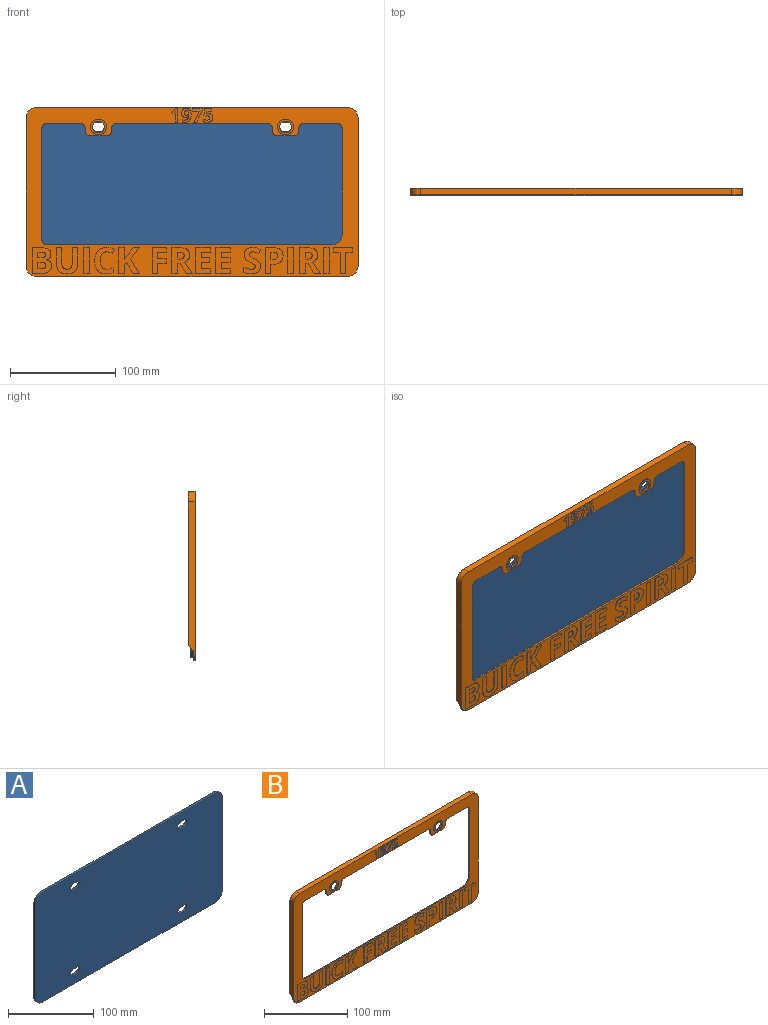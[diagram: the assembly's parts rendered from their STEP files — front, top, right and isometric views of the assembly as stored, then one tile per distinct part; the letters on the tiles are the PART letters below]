
ASSEMBLY  parts=2 mates=1
PART A: 26 faces, bbox 308x3x156 mm
  f0: plane 284x3mm, normal (0,0,1), area 852mm2, adj f1,f23,f24,f25
  f1: cylinder r=12mm len=12mm, axis (0,1,0), area 56.5mm2, adj f0,f2,f24,f25
  f2: plane 132x3mm, normal (-1,0,0), area 396mm2, adj f1,f3,f24,f25
  f3: cylinder r=12mm len=12mm, axis (0,1,0), area 56.5mm2, adj f2,f4,f24,f25
  f4: plane 284x3mm, normal (0,0,-1), area 852mm2, adj f3,f5,f24,f25
  f5: cylinder r=12mm len=12mm, axis (0,1,0), area 56.5mm2, adj f4,f6,f24,f25
  f6: plane 132x3mm, normal (1,0,0), area 396mm2, adj f5,f23,f24,f25
  f7: plane 8x3mm, normal (0,0,-1), area 24mm2, adj f8,f19,f24,f25
  f8: cylinder r=4.25mm len=8.5mm, axis (0,1,0), area 40.1mm2, adj f7,f9,f24,f25
  f9: plane 8x3mm, normal (0,0,1), area 24mm2, adj f8,f19,f24,f25
  f10: cylinder r=4.25mm len=8.5mm, axis (0,1,0), area 40.1mm2, adj f11,f20,f24,f25
  f11: plane 8x3mm, normal (0,0,1), area 24mm2, adj f10,f12,f24,f25
  f12: cylinder r=4.25mm len=8.5mm, axis (0,1,0), area 40.1mm2, adj f11,f20,f24,f25
  f13: plane 8x3mm, normal (0,0,-1), area 24mm2, adj f14,f21,f24,f25
  f14: cylinder r=4.25mm len=8.5mm, axis (0,1,0), area 40.1mm2, adj f13,f15,f24,f25
  f15: plane 8x3mm, normal (0,0,1), area 24mm2, adj f14,f21,f24,f25
  f16: cylinder r=4.25mm len=8.5mm, axis (0,1,0), area 40.1mm2, adj f17,f22,f24,f25
  f17: plane 8x3mm, normal (0,0,-1), area 24mm2, adj f16,f18,f24,f25
  f18: cylinder r=4.25mm len=8.5mm, axis (0,1,0), area 40.1mm2, adj f17,f22,f24,f25
  f19: cylinder r=4.25mm len=8.5mm, axis (0,1,0), area 40.1mm2, adj f7,f9,f24,f25
  f20: plane 8x3mm, normal (0,0,-1), area 24mm2, adj f10,f12,f24,f25
  f21: cylinder r=4.25mm len=8.5mm, axis (0,1,0), area 40.1mm2, adj f13,f15,f24,f25
  f22: plane 8x3mm, normal (0,0,1), area 24mm2, adj f16,f18,f24,f25
  f23: cylinder r=12mm len=12mm, axis (0,1,0), area 56.5mm2, adj f0,f6,f24,f25
  f24: plane 308x156mm, normal (0,-1,0), area 47425.4mm2, adj f0,f1,f2,f3,f4,f5,f6,f7
  f25: plane 308x156mm, normal (0,1,0), area 47425.4mm2, adj f0,f1,f2,f3,f4,f5,f6,f7
PART B: 350 faces, bbox 314x7x160 mm
  f0: plane 140x4.8mm, normal (1,0,0), area 564mm2, adj f1,f329,f334,f335,f340,f342,f343,f345
  f1: plane 314x158mm, normal (0,1,0), area 16737.1mm2, adj f0,f3,f4,f8,f9,f10,f12,f13
  f2: plane 314x160mm, normal (0,-1,0), area 13997.6mm2, adj f3,f4,f5,f6,f7,f8,f9,f10
  f3: plane 142x1.6mm, normal (0,0,-1), area 227.2mm2, adj f1,f2,f27,f33
  f4: plane 31x1.6mm, normal (0,0,-1), area 49.6mm2, adj f1,f2,f14,f31
  f5: plane 294x6.4mm, normal (0,0,1), area 1881.6mm2, adj f2,f6,f20,f335
  f6: cylinder r=10mm len=10mm, axis (0,1,0), area 100.5mm2, adj f2,f5,f7,f335
  f7: plane 140x6.4mm, normal (-1,0,0), area 887.2mm2, adj f2,f6,f8,f329,f335,f345
  f8: cylinder r=10mm len=10mm, axis (0,1,0), area 25.1mm2, adj f1,f2,f7,f9
  f9: plane 294x1.6mm, normal (0,0,-1), area 470.4mm2, adj f1,f2,f8,f10
  f10: cylinder r=10mm len=10mm, axis (0,1,0), area 25.1mm2, adj f1,f2,f9,f11
  f11: plane 140x6.4mm, normal (1,0,0), area 887.2mm2, adj f2,f10,f20,f330,f335,f344
  f12: cylinder r=5mm len=5mm, axis (0,1,0), area 12.6mm2, adj f1,f2,f13,f19
  f13: plane 105x1.6mm, normal (1,0,0), area 168mm2, adj f1,f2,f12,f14
  f14: cylinder r=5mm len=5mm, axis (0,1,0), area 12.6mm2, adj f1,f2,f4,f13
  f15: plane 31x1.6mm, normal (0,0,-1), area 49.6mm2, adj f1,f2,f16,f29
  f16: cylinder r=5mm len=5mm, axis (0,1,0), area 12.6mm2, adj f1,f2,f15,f17
  f17: plane 100x1.6mm, normal (-1,0,0), area 160mm2, adj f1,f2,f16,f18
  f18: cylinder r=10mm len=10mm, axis (0,1,0), area 25.1mm2, adj f1,f2,f17,f19
  f19: plane 269x1.6mm, normal (0,0,1), area 430.4mm2, adj f1,f2,f12,f18
  f20: cylinder r=10mm len=10mm, axis (0,1,0), area 100.5mm2, adj f2,f5,f11,f335
  f21: plane 2x1.6mm, normal (-1,0,0), area 3.2mm2, adj f1,f2,f31,f32
  f22: plane 15x1.6mm, normal (0,0,-1), area 24mm2, adj f1,f2,f32,f34
  f23: plane 2x1.6mm, normal (1,0,0), area 3.2mm2, adj f1,f2,f33,f34
  f24: plane 2x1.6mm, normal (-1,0,0), area 3.2mm2, adj f1,f2,f27,f28
  f25: plane 15x1.6mm, normal (0,0,-1), area 24mm2, adj f1,f2,f28,f30
  f26: plane 2x1.6mm, normal (1,0,0), area 3.2mm2, adj f1,f2,f29,f30
  f27: cylinder r=5mm len=5mm, axis (0,1,0), area 12.6mm2, adj f1,f2,f3,f24
  f28: cylinder r=5mm len=5mm, axis (0,-1,0), area 12.6mm2, adj f1,f2,f24,f25
  f29: cylinder r=5mm len=5mm, axis (0,-1,0), area 12.6mm2, adj f1,f2,f15,f26
  f30: cylinder r=5mm len=5mm, axis (0,1,0), area 12.6mm2, adj f1,f2,f25,f26
  f31: cylinder r=5mm len=5mm, axis (0,1,0), area 12.6mm2, adj f1,f2,f4,f21
  f32: cylinder r=5mm len=5mm, axis (0,-1,0), area 12.6mm2, adj f1,f2,f21,f22
  f33: cylinder r=5mm len=5mm, axis (0,-1,0), area 12.6mm2, adj f1,f2,f3,f23
  f34: cylinder r=5mm len=5mm, axis (0,1,0), area 12.6mm2, adj f1,f2,f22,f23
  f35: cylinder r=5.5mm len=11mm, axis (0,-1,0), area 76mm2, adj f1,f349
  f36: cylinder r=5.5mm len=11mm, axis (0,-1,0), area 76mm2, adj f1,f347
  f37: plane 2.73x0.6mm, normal (0,0,-1), area 1.6mm2, adj f2,f38,f46,f47
  f38: plane 12.89x0.6mm, normal (1,0,0), area 7.7mm2, adj f2,f37,f39,f47
  f39: plane 2.24x0.6mm, normal (0,0,1), area 1.3mm2, adj f2,f38,f40,f47
  f40: plane 4.15x3.31mm, normal (-0.62,0,0.78), area 3.2mm2, adj f2,f39,f41,f47
  f41: plane 1.64x1.31mm, normal (-0.78,0,-0.63), area 1.3mm2, adj f2,f40,f42,f47
  f42: plane 1.48x1.19mm, normal (0.63,0,-0.78), area 1.1mm2, adj f2,f41,f43,f47
  f43: extruded ~0.94x0.89mm, area 0.8mm2, adj f2,f42,f44,f47
  f44: plane 1.34x0.6mm, normal (-1,0,0.03), area 0.8mm2, adj f2,f43,f45,f47
  f45: plane 1.22x0.6mm, normal (-1,0,0.02), area 0.7mm2, adj f2,f44,f46,f47
  f46: plane 7.46x0.6mm, normal (-1,0,0), area 4.5mm2, adj f2,f37,f45,f47
  f47: plane 12.89x6.39mm, normal (0,-1,0), area 43mm2, adj f37,f38,f39,f40,f41,f42,f43,f44
  f48: extruded ~1.32x0.6mm, area 0.9mm2, adj f49,f73,f74,f75
  f49: extruded ~1.41x0.72mm, area 1mm2, adj f48,f50,f74,f75
  f50: extruded ~1.77x0.6mm, area 1.1mm2, adj f49,f51,f74,f75
  f51: extruded ~1.25x0.6mm, area 0.9mm2, adj f50,f52,f74,f75
  f52: extruded ~1.42x0.6mm, area 0.9mm2, adj f51,f53,f74,f75
  f53: extruded ~1.31x0.6mm, area 0.9mm2, adj f52,f54,f74,f75
  f54: extruded ~1.48x0.6mm, area 0.9mm2, adj f53,f73,f74,f75
  f55: extruded ~5.69x1.6mm, area 3.6mm2, adj f2,f56,f72,f74
  f56: extruded ~3.04x0.6mm, area 1.9mm2, adj f2,f55,f57,f74
  f57: extruded ~1.94x1.64mm, area 1.6mm2, adj f2,f56,f58,f74
  f58: extruded ~2.5x0.67mm, area 1.6mm2, adj f2,f57,f59,f74
  f59: extruded ~3.2x1.2mm, area 2.1mm2, adj f2,f58,f60,f74
  f60: extruded ~3.28x1.18mm, area 2.1mm2, adj f2,f59,f61,f74
  f61: extruded ~3x0.97mm, area 1.9mm2, adj f2,f60,f62,f74
  f62: extruded ~2.65x1.08mm, area 1.8mm2, adj f2,f61,f63,f74
  f63: extruded ~1.67x0.6mm, area 1mm2, adj f2,f62,f64,f74
  f64: extruded ~1.18x1.16mm, area 1mm2, adj f2,f63,f65,f74
  f65: plane 0.6x0.11mm, normal (0,0,-1), area 0.1mm2, adj f2,f64,f66,f74
  f66: extruded ~2.37x0.6mm, area 1.5mm2, adj f2,f65,f67,f74
  f67: extruded ~1.35x1.26mm, area 1.1mm2, adj f2,f66,f68,f74
  f68: extruded ~2.25x0.6mm, area 1.4mm2, adj f2,f67,f69,f74
  f69: extruded ~1.55x0.6mm, area 0.9mm2, adj f2,f68,f70,f74
  f70: plane 2.19x0.6mm, normal (-1,0,0), area 1.3mm2, adj f2,f69,f71,f74
  f71: extruded ~1.74x0.6mm, area 1mm2, adj f2,f70,f72,f74
  f72: extruded ~4.86x1.88mm, area 3.2mm2, adj f2,f55,f71,f74
  f73: extruded ~1.67x0.6mm, area 1.1mm2, adj f48,f54,f74,f75
  f74: plane 13.22x9.1mm, normal (0,-1,0), area 70.9mm2, adj f48,f49,f50,f51,f52,f53,f54,f55
  f75: plane 4.29x3.76mm, normal (0,-1,0), area 13mm2, adj f48,f49,f50,f51,f52,f53,f54,f73
  f76: plane 10.58x4.84mm, normal (-0.91,0,0.42), area 7mm2, adj f2,f77,f82,f83
  f77: plane 2.86x0.6mm, normal (0,0,-1), area 1.7mm2, adj f2,f76,f78,f83
  f78: plane 11.16x4.88mm, normal (0.92,0,-0.4), area 7.3mm2, adj f2,f77,f79,f83
  f79: plane 1.71x0.6mm, normal (1,0,0), area 1mm2, adj f2,f78,f80,f83
  f80: plane 9.25x0.6mm, normal (0,0,1), area 5.5mm2, adj f2,f79,f81,f83
  f81: plane 2.29x0.6mm, normal (-1,0,0), area 1.4mm2, adj f2,f80,f82,f83
  f82: plane 6.36x0.6mm, normal (0,0,-1), area 3.8mm2, adj f2,f76,f81,f83
  f83: plane 12.87x9.25mm, normal (0,-1,0), area 50.2mm2, adj f76,f77,f78,f79,f80,f81,f82
  f84: extruded ~2.98x1.05mm, area 1.9mm2, adj f2,f85,f103,f104
  f85: extruded ~1.33x0.6mm, area 0.8mm2, adj f2,f84,f86,f104
  f86: plane 0.6x0.31mm, normal (-0.2,0,0.98), area 0.2mm2, adj f2,f85,f87,f104
  f87: plane 2.53x0.6mm, normal (1,0,-0.09), area 1.5mm2, adj f2,f86,f88,f104
  f88: plane 4.6x0.6mm, normal (0,0,-1), area 2.8mm2, adj f2,f87,f89,f104
  f89: plane 2.31x0.6mm, normal (1,0,0), area 1.4mm2, adj f2,f88,f90,f104
  f90: plane 6.99x0.6mm, normal (0,0,1), area 4.2mm2, adj f2,f89,f91,f104
  f91: plane 6.57x0.6mm, normal (-1,0,0.07), area 4mm2, adj f2,f90,f92,f104
  f92: plane 1.09x0.6mm, normal (-0.47,0,-0.88), area 0.7mm2, adj f2,f91,f93,f104
  f93: extruded ~0.92x0.6mm, area 0.6mm2, adj f2,f92,f94,f104
  f94: extruded ~1.03x0.6mm, area 0.6mm2, adj f2,f93,f95,f104
  f95: extruded ~2.58x1.95mm, area 2.2mm2, adj f2,f94,f96,f104
  f96: extruded ~2.5x2.05mm, area 2.2mm2, adj f2,f95,f97,f104
  f97: extruded ~1.75x0.6mm, area 1.1mm2, adj f2,f96,f98,f104
  f98: extruded ~1.62x0.6mm, area 1mm2, adj f2,f97,f99,f104
  f99: plane 2.36x0.6mm, normal (-1,0,0), area 1.4mm2, adj f2,f98,f100,f104
  f100: extruded ~3.47x0.7mm, area 2.1mm2, adj f2,f99,f101,f104
  f101: extruded ~3.81x1.17mm, area 2.4mm2, adj f2,f100,f102,f104
  f102: extruded ~3.32x1.33mm, area 2.2mm2, adj f2,f101,f103,f104
  f103: extruded ~2.87x1.11mm, area 1.9mm2, adj f2,f84,f102,f104
  f104: plane 13.07x8.61mm, normal (0,-1,0), area 65.6mm2, adj f84,f85,f86,f87,f88,f89,f90,f91
  f105: plane 6.34x0.6mm, normal (1,0,0), area 3.8mm2, adj f106,f129,f130,f131
  f106: plane 3.2x0.6mm, normal (0,0,-1), area 1.9mm2, adj f105,f107,f130,f131
  f107: extruded ~4.33x3.03mm, area 3.6mm2, adj f106,f108,f130,f131
  f108: extruded ~2.5x1.02mm, area 1.7mm2, adj f107,f109,f130,f131
  f109: extruded ~3.15x0.82mm, area 2mm2, adj f108,f129,f130,f131
  f110: plane 2.99x0.6mm, normal (0,0,1), area 1.8mm2, adj f111,f127,f130,f132
  f111: plane 5.41x0.6mm, normal (1,0,0), area 3.2mm2, adj f110,f112,f130,f132
  f112: plane 2.71x0.6mm, normal (0,0,-1), area 1.6mm2, adj f111,f113,f130,f132
  f113: extruded ~3.24x0.61mm, area 2mm2, adj f112,f114,f130,f132
  f114: extruded ~2.01x1.02mm, area 1.4mm2, adj f113,f115,f130,f132
  f115: extruded ~2.15x0.94mm, area 1.5mm2, adj f114,f127,f130,f132
  f116: plane 7.58x0.6mm, normal (0,0,1), area 4.5mm2, adj f2,f117,f128,f130
  f117: plane 24.34x0.6mm, normal (-1,0,0), area 14.6mm2, adj f2,f116,f118,f130
  f118: plane 9.1x0.6mm, normal (0,0,-1), area 5.5mm2, adj f2,f117,f119,f130
  f119: extruded ~6.54x1.86mm, area 4.2mm2, adj f2,f118,f120,f130
  f120: extruded ~5.19x2.41mm, area 3.6mm2, adj f2,f119,f121,f130
  f121: extruded ~3.76x1.03mm, area 2.4mm2, adj f2,f120,f122,f130
  f122: extruded ~3.34x1.93mm, area 2.4mm2, adj f2,f121,f123,f130
  f123: plane 0.6x0.17mm, normal (1,0,0), area 0.1mm2, adj f2,f122,f124,f130
  f124: extruded ~2.72x1.68mm, area 2mm2, adj f2,f123,f125,f130
  f125: extruded ~3.58x1.02mm, area 2.3mm2, adj f2,f124,f126,f130
  f126: extruded ~4.69x2.34mm, area 3.3mm2, adj f2,f125,f128,f130
  f127: extruded ~3.04x0.65mm, area 1.9mm2, adj f110,f115,f130,f132
  f128: extruded ~7.52x1.47mm, area 4.7mm2, adj f2,f116,f126,f130
  f129: plane 3.36x0.6mm, normal (0,0,1), area 2mm2, adj f105,f109,f130,f131
  f130: plane 24.34x18.05mm, normal (0,-1,0), area 323mm2, adj f105,f106,f107,f108,f109,f110,f111,f112
  f131: plane 7.52x6.34mm, normal (0,-1,0), area 43.3mm2, adj f105,f106,f107,f108,f109,f129
  f132: plane 6.97x5.41mm, normal (0,-1,0), area 34.4mm2, adj f110,f111,f112,f113,f114,f115,f127
  f133: plane 15.75x0.6mm, normal (1,0,0), area 9.4mm2, adj f2,f134,f147,f148
  f134: plane 5.15x0.6mm, normal (0,0,1), area 3.1mm2, adj f2,f133,f135,f148
  f135: plane 14.87x0.6mm, normal (-1,0,0), area 8.9mm2, adj f2,f134,f136,f148
  f136: extruded ~4.15x1.14mm, area 2.6mm2, adj f2,f135,f137,f148
  f137: extruded ~3.67x1.32mm, area 2.4mm2, adj f2,f136,f138,f148
  f138: extruded ~3.75x1.32mm, area 2.5mm2, adj f2,f137,f139,f148
  f139: extruded ~4.13x1.13mm, area 2.6mm2, adj f2,f138,f140,f148
  f140: plane 14.9x0.6mm, normal (1,0,0), area 8.9mm2, adj f2,f139,f141,f148
  f141: plane 5.14x0.6mm, normal (0,0,1), area 3.1mm2, adj f2,f140,f142,f148
  f142: plane 15.68x0.6mm, normal (-1,0,0), area 9.4mm2, adj f2,f141,f143,f148
  f143: extruded ~6.58x2.6mm, area 4.4mm2, adj f2,f142,f144,f148
  f144: extruded ~7.29x2.41mm, area 4.7mm2, adj f2,f143,f145,f148
  f145: extruded ~5.39x1.08mm, area 3.3mm2, adj f2,f144,f146,f148
  f146: extruded ~3.49x3.11mm, area 2.8mm2, adj f2,f145,f147,f148
  f147: extruded ~4.73x1.21mm, area 3mm2, adj f2,f133,f146,f148
  f148: plane 24.68x19.98mm, normal (0,-1,0), area 271.1mm2, adj f133,f134,f135,f136,f137,f138,f139,f140
  f149: plane 24.34x0.6mm, normal (-1,0,0), area 14.6mm2, adj f2,f150,f152,f153
  f150: plane 5.16x0.6mm, normal (0,0,-1), area 3.1mm2, adj f2,f149,f151,f153
  f151: plane 24.34x0.6mm, normal (1,0,0), area 14.6mm2, adj f2,f150,f152,f153
  f152: plane 5.16x0.6mm, normal (0,0,1), area 3.1mm2, adj f2,f149,f151,f153
  f153: plane 24.34x5.16mm, normal (0,-1,0), area 125.6mm2, adj f149,f150,f151,f152
  f154: extruded ~4.51x2.19mm, area 3.1mm2, adj f2,f155,f168,f169
  f155: extruded ~2.71x0.6mm, area 1.7mm2, adj f2,f154,f156,f169
  f156: extruded ~2.75x1.13mm, area 1.8mm2, adj f2,f155,f157,f169
  f157: plane 4.2x1.66mm, normal (0.93,0,-0.37), area 2.7mm2, adj f2,f156,f158,f169
  f158: extruded ~7.12x1.71mm, area 4.4mm2, adj f2,f157,f159,f169
  f159: extruded ~6.07x1.52mm, area 3.8mm2, adj f2,f158,f160,f169
  f160: extruded ~4.38x3.97mm, area 3.6mm2, adj f2,f159,f161,f169
  f161: extruded ~6.65x1.38mm, area 4.1mm2, adj f2,f160,f162,f169
  f162: extruded ~9.25x2.81mm, area 5.9mm2, adj f2,f161,f163,f169
  f163: extruded ~8.12x3.22mm, area 5.4mm2, adj f2,f162,f164,f169
  f164: extruded ~6.69x1.25mm, area 4.1mm2, adj f2,f163,f165,f169
  f165: plane 4.33x0.6mm, normal (1,0,0), area 2.6mm2, adj f2,f164,f166,f169
  f166: extruded ~6.21x1.28mm, area 3.8mm2, adj f2,f165,f167,f169
  f167: extruded ~8.14x6.11mm, area 7mm2, adj f2,f166,f168,f169
  f168: extruded ~6.1x1.6mm, area 3.8mm2, adj f2,f154,f167,f169
  f169: plane 25.02x18.54mm, normal (0,-1,0), area 208mm2, adj f154,f155,f156,f157,f158,f159,f160,f161
  f170: plane 5.86x0.6mm, normal (0,0,-1), area 3.5mm2, adj f2,f171,f182,f183
  f171: plane 13.57x8.56mm, normal (0.85,0,0.53), area 9.6mm2, adj f2,f170,f172,f183
  f172: plane 10.77x8.49mm, normal (0.79,0,-0.62), area 8.2mm2, adj f2,f171,f173,f183
  f173: plane 5.73x0.6mm, normal (0,0,1), area 3.4mm2, adj f2,f172,f174,f183
  f174: plane 8.27x6.6mm, normal (-0.78,0,0.62), area 6.3mm2, adj f2,f173,f175,f183
  f175: plane 2.87x2.03mm, normal (-0.82,0,0.58), area 2.1mm2, adj f2,f174,f176,f183
  f176: plane 11.14x0.6mm, normal (1,0,0), area 6.7mm2, adj f2,f175,f177,f183
  f177: plane 5.16x0.6mm, normal (0,0,1), area 3.1mm2, adj f2,f176,f178,f183
  f178: plane 24.34x0.6mm, normal (-1,0,0), area 14.6mm2, adj f2,f177,f179,f183
  f179: plane 5.16x0.6mm, normal (0,0,-1), area 3.1mm2, adj f2,f178,f180,f183
  f180: plane 8.69x0.6mm, normal (1,0,0), area 5.2mm2, adj f2,f179,f181,f183
  f181: plane 2.18x1.57mm, normal (0.58,0,-0.81), area 1.6mm2, adj f2,f180,f182,f183
  f182: plane 10.25x6.38mm, normal (-0.85,0,-0.53), area 7.2mm2, adj f2,f170,f181,f183
  f183: plane 24.34x19.58mm, normal (0,-1,0), area 271.7mm2, adj f170,f171,f172,f173,f174,f175,f176,f177
  f184: plane 5.08x0.6mm, normal (0,0,-1), area 3mm2, adj f2,f185,f193,f194
  f185: plane 9.62x0.6mm, normal (1,0,0), area 5.8mm2, adj f2,f184,f186,f194
  f186: plane 8.26x0.6mm, normal (0,0,-1), area 5mm2, adj f2,f185,f187,f194
  f187: plane 4.21x0.6mm, normal (1,0,0), area 2.5mm2, adj f2,f186,f188,f194
  f188: plane 8.26x0.6mm, normal (0,0,1), area 5mm2, adj f2,f187,f189,f194
  f189: plane 6.28x0.6mm, normal (1,0,0), area 3.8mm2, adj f2,f188,f190,f194
  f190: plane 8.88x0.6mm, normal (0,0,-1), area 5.3mm2, adj f2,f189,f191,f194
  f191: plane 4.23x0.6mm, normal (1,0,0), area 2.5mm2, adj f2,f190,f192,f194
  f192: plane 13.95x0.6mm, normal (0,0,1), area 8.4mm2, adj f2,f191,f193,f194
  f193: plane 24.34x0.6mm, normal (-1,0,0), area 14.6mm2, adj f2,f184,f192,f194
  f194: plane 24.34x13.95mm, normal (0,-1,0), area 195.9mm2, adj f184,f185,f186,f187,f188,f189,f190,f191
  f195: plane 9.34x0.6mm, normal (1,0,0), area 5.6mm2, adj f2,f196,f213,f214
  f196: plane 2.74x0.6mm, normal (0,0,-1), area 1.6mm2, adj f2,f195,f197,f214
  f197: plane 9.34x5.81mm, normal (-0.85,0,-0.53), area 6.6mm2, adj f2,f196,f198,f214
  f198: plane 5.73x0.6mm, normal (0,0,-1), area 3.4mm2, adj f2,f197,f199,f214
  f199: extruded ~10.61x7.16mm, area 7.7mm2, adj f2,f198,f200,f214
  f200: extruded ~3.35x2.62mm, area 2.6mm2, adj f2,f199,f201,f214
  f201: extruded ~3.82x1.18mm, area 2.4mm2, adj f2,f200,f202,f214
  f202: extruded ~5.49x2.38mm, area 3.7mm2, adj f2,f201,f203,f214
  f203: extruded ~7.34x1.81mm, area 4.6mm2, adj f2,f202,f204,f214
  f204: plane 7.09x0.6mm, normal (0,0,1), area 4.3mm2, adj f2,f203,f205,f214
  f205: plane 24.34x0.6mm, normal (-1,0,0), area 14.6mm2, adj f2,f204,f213,f214
  f206: plane 1.66x0.6mm, normal (0,0,1), area 1mm2, adj f207,f212,f214,f215
  f207: plane 6.57x0.6mm, normal (1,0,0), area 3.9mm2, adj f206,f208,f214,f215
  f208: plane 1.57x0.6mm, normal (0,0,-1), area 0.9mm2, adj f207,f209,f214,f215
  f209: extruded ~3.68x0.73mm, area 2.3mm2, adj f208,f210,f214,f215
  f210: extruded ~2.46x1.19mm, area 1.7mm2, adj f209,f211,f214,f215
  f211: extruded ~2.56x1.16mm, area 1.8mm2, adj f210,f212,f214,f215
  f212: extruded ~3.61x0.82mm, area 2.3mm2, adj f206,f211,f214,f215
  f213: plane 5.16x0.6mm, normal (0,0,-1), area 3.1mm2, adj f2,f195,f205,f214
  f214: plane 24.34x19.44mm, normal (0,-1,0), area 289.3mm2, adj f195,f196,f197,f198,f199,f200,f201,f202
  f215: plane 6.57x6.44mm, normal (0,-1,0), area 37.4mm2, adj f206,f207,f208,f209,f210,f211,f212
  f216: plane 14.02x0.6mm, normal (0,0,-1), area 8.4mm2, adj f2,f217,f227,f228
  f217: plane 4.26x0.6mm, normal (1,0,0), area 2.6mm2, adj f2,f216,f218,f228
  f218: plane 8.85x0.6mm, normal (0,0,1), area 5.3mm2, adj f2,f217,f219,f228
  f219: plane 6.28x0.6mm, normal (1,0,0), area 3.8mm2, adj f2,f218,f220,f228
  f220: plane 8.24x0.6mm, normal (0,0,-1), area 4.9mm2, adj f2,f219,f221,f228
  f221: plane 4.23x0.6mm, normal (1,0,0), area 2.5mm2, adj f2,f220,f222,f228
  f222: plane 8.24x0.6mm, normal (0,0,1), area 4.9mm2, adj f2,f221,f223,f228
  f223: plane 5.34x0.6mm, normal (1,0,0), area 3.2mm2, adj f2,f222,f224,f228
  f224: plane 8.85x0.6mm, normal (0,0,-1), area 5.3mm2, adj f2,f223,f225,f228
  f225: plane 4.23x0.6mm, normal (1,0,0), area 2.5mm2, adj f2,f224,f226,f228
  f226: plane 14.02x0.6mm, normal (0,0,1), area 8.4mm2, adj f2,f225,f227,f228
  f227: plane 24.34x0.6mm, normal (-1,0,0), area 14.6mm2, adj f2,f216,f226,f228
  f228: plane 24.34x14.02mm, normal (0,-1,0), area 235.7mm2, adj f216,f217,f218,f219,f220,f221,f222,f223
  f229: plane 14.02x0.6mm, normal (0,0,-1), area 8.4mm2, adj f2,f230,f240,f241
  f230: plane 4.26x0.6mm, normal (1,0,0), area 2.6mm2, adj f2,f229,f231,f241
  f231: plane 8.85x0.6mm, normal (0,0,1), area 5.3mm2, adj f2,f230,f232,f241
  f232: plane 6.28x0.6mm, normal (1,0,0), area 3.8mm2, adj f2,f231,f233,f241
  f233: plane 8.24x0.6mm, normal (0,0,-1), area 4.9mm2, adj f2,f232,f234,f241
  f234: plane 4.23x0.6mm, normal (1,0,0), area 2.5mm2, adj f2,f233,f235,f241
  f235: plane 8.24x0.6mm, normal (0,0,1), area 4.9mm2, adj f2,f234,f236,f241
  f236: plane 5.34x0.6mm, normal (1,0,0), area 3.2mm2, adj f2,f235,f237,f241
  f237: plane 8.85x0.6mm, normal (0,0,-1), area 5.3mm2, adj f2,f236,f238,f241
  f238: plane 4.23x0.6mm, normal (1,0,0), area 2.5mm2, adj f2,f237,f239,f241
  f239: plane 14.02x0.6mm, normal (0,0,1), area 8.4mm2, adj f2,f238,f240,f241
  f240: plane 24.34x0.6mm, normal (-1,0,0), area 14.6mm2, adj f2,f229,f239,f241
  f241: plane 24.34x14.02mm, normal (0,-1,0), area 235.7mm2, adj f229,f230,f231,f232,f233,f234,f235,f236
  f242: extruded ~5.2x2.37mm, area 3.6mm2, adj f2,f243,f269,f270
  f243: extruded ~4.02x1.27mm, area 2.6mm2, adj f2,f242,f244,f270
  f244: extruded ~4.68x3.27mm, area 3.5mm2, adj f2,f243,f245,f270
  f245: extruded ~3.27x1.7mm, area 2.2mm2, adj f2,f244,f246,f270
  f246: extruded ~1.01x0.98mm, area 0.9mm2, adj f2,f245,f247,f270
  f247: extruded ~1.19x0.6mm, area 0.7mm2, adj f2,f246,f248,f270
  f248: extruded ~1.78x0.78mm, area 1.2mm2, adj f2,f247,f249,f270
  f249: extruded ~2.25x0.68mm, area 1.4mm2, adj f2,f248,f250,f270
  f250: extruded ~2.5x0.6mm, area 1.5mm2, adj f2,f249,f251,f270
  f251: extruded ~3.22x1.12mm, area 2mm2, adj f2,f250,f252,f270
  f252: plane 4.02x1.66mm, normal (0.92,0,-0.38), area 2.6mm2, adj f2,f251,f253,f270
  f253: extruded ~3.6x1.26mm, area 2.3mm2, adj f2,f252,f254,f270
  f254: extruded ~3.62x0.6mm, area 2.2mm2, adj f2,f253,f255,f270
  f255: extruded ~6.05x1.85mm, area 3.9mm2, adj f2,f254,f256,f270
  f256: extruded ~5.08x2.19mm, area 3.4mm2, adj f2,f255,f257,f270
  f257: extruded ~2.99x0.67mm, area 1.9mm2, adj f2,f256,f258,f270
  f258: extruded ~2.25x1.78mm, area 1.7mm2, adj f2,f257,f259,f270
  f259: extruded ~3.34x2.01mm, area 2.3mm2, adj f2,f258,f260,f270
  f260: extruded ~3.16x1.65mm, area 2.1mm2, adj f2,f259,f261,f270
  f261: extruded ~1.17x1.07mm, area 1mm2, adj f2,f260,f262,f270
  f262: extruded ~1.27x0.6mm, area 0.8mm2, adj f2,f261,f263,f270
  f263: extruded ~1.93x0.91mm, area 1.3mm2, adj f2,f262,f264,f270
  f264: extruded ~2.6x0.65mm, area 1.6mm2, adj f2,f263,f265,f270
  f265: extruded ~3.12x0.6mm, area 1.9mm2, adj f2,f264,f266,f270
  f266: extruded ~4.17x1.55mm, area 2.7mm2, adj f2,f265,f267,f270
  f267: plane 4.79x0.6mm, normal (-1,0,0), area 2.9mm2, adj f2,f266,f268,f270
  f268: extruded ~6.89x1.47mm, area 4.3mm2, adj f2,f267,f269,f270
  f269: extruded ~6.6x1.9mm, area 4.2mm2, adj f2,f242,f268,f270
  f270: plane 25.02x15.86mm, normal (0,-1,0), area 223.4mm2, adj f242,f243,f244,f245,f246,f247,f248,f249
  f271: extruded ~6.01x2.46mm, area 4mm2, adj f2,f272,f286,f287
  f272: extruded ~5.68x2.3mm, area 3.8mm2, adj f2,f271,f273,f287
  f273: extruded ~6.74x1.91mm, area 4.3mm2, adj f2,f272,f274,f287
  f274: plane 7.77x0.6mm, normal (0,0,1), area 4.7mm2, adj f2,f273,f275,f287
  f275: plane 24.34x0.6mm, normal (-1,0,0), area 14.6mm2, adj f2,f274,f276,f287
  f276: plane 5.16x0.6mm, normal (0,0,-1), area 3.1mm2, adj f2,f275,f277,f287
  f277: plane 8.66x0.6mm, normal (1,0,0), area 5.2mm2, adj f2,f276,f278,f287
  f278: plane 2.21x0.6mm, normal (0,0,-1), area 1.3mm2, adj f2,f277,f286,f287
  f279: plane 1.7x0.6mm, normal (0,0,1), area 1mm2, adj f280,f285,f287,f288
  f280: plane 7.22x0.6mm, normal (1,0,0), area 4.3mm2, adj f279,f281,f287,f288
  f281: plane 2.34x0.6mm, normal (0,0,-1), area 1.4mm2, adj f280,f282,f287,f288
  f282: extruded ~3.11x0.87mm, area 2mm2, adj f281,f283,f287,f288
  f283: extruded ~2.68x0.99mm, area 1.8mm2, adj f282,f284,f287,f288
  f284: extruded ~2.74x1.18mm, area 1.9mm2, adj f283,f285,f287,f288
  f285: extruded ~3.56x0.94mm, area 2.2mm2, adj f279,f284,f287,f288
  f286: extruded ~6.98x2.08mm, area 4.5mm2, adj f2,f271,f278,f287
  f287: plane 24.34x16.81mm, normal (0,-1,0), area 242.1mm2, adj f271,f272,f273,f274,f275,f276,f277,f278
  f288: plane 7.22x6.44mm, normal (0,-1,0), area 41.3mm2, adj f279,f280,f281,f282,f283,f284,f285
  f289: plane 24.34x0.6mm, normal (-1,0,0), area 14.6mm2, adj f2,f290,f292,f293
  f290: plane 5.16x0.6mm, normal (0,0,-1), area 3.1mm2, adj f2,f289,f291,f293
  f291: plane 24.34x0.6mm, normal (1,0,0), area 14.6mm2, adj f2,f290,f292,f293
  f292: plane 5.16x0.6mm, normal (0,0,1), area 3.1mm2, adj f2,f289,f291,f293
  f293: plane 24.34x5.16mm, normal (0,-1,0), area 125.6mm2, adj f289,f290,f291,f292
  f294: plane 9.34x0.6mm, normal (1,0,0), area 5.6mm2, adj f2,f295,f312,f313
  f295: plane 2.74x0.6mm, normal (0,0,-1), area 1.6mm2, adj f2,f294,f296,f313
  f296: plane 9.34x5.81mm, normal (-0.85,0,-0.53), area 6.6mm2, adj f2,f295,f297,f313
  f297: plane 5.73x0.6mm, normal (0,0,-1), area 3.4mm2, adj f2,f296,f298,f313
  f298: extruded ~10.61x7.16mm, area 7.7mm2, adj f2,f297,f299,f313
  f299: extruded ~3.35x2.62mm, area 2.6mm2, adj f2,f298,f300,f313
  f300: extruded ~3.82x1.18mm, area 2.4mm2, adj f2,f299,f301,f313
  f301: extruded ~5.49x2.38mm, area 3.7mm2, adj f2,f300,f302,f313
  f302: extruded ~7.34x1.81mm, area 4.6mm2, adj f2,f301,f303,f313
  f303: plane 7.09x0.6mm, normal (0,0,1), area 4.3mm2, adj f2,f302,f304,f313
  f304: plane 24.34x0.6mm, normal (-1,0,0), area 14.6mm2, adj f2,f303,f312,f313
  f305: plane 1.66x0.6mm, normal (0,0,1), area 1mm2, adj f306,f311,f313,f314
  f306: plane 6.57x0.6mm, normal (1,0,0), area 3.9mm2, adj f305,f307,f313,f314
  f307: plane 1.57x0.6mm, normal (0,0,-1), area 0.9mm2, adj f306,f308,f313,f314
  f308: extruded ~3.68x0.73mm, area 2.3mm2, adj f307,f309,f313,f314
  f309: extruded ~2.46x1.19mm, area 1.7mm2, adj f308,f310,f313,f314
  f310: extruded ~2.56x1.16mm, area 1.8mm2, adj f309,f311,f313,f314
  f311: extruded ~3.61x0.82mm, area 2.3mm2, adj f305,f310,f313,f314
  f312: plane 5.16x0.6mm, normal (0,0,-1), area 3.1mm2, adj f2,f294,f304,f313
  f313: plane 24.34x19.44mm, normal (0,-1,0), area 289.3mm2, adj f294,f295,f296,f297,f298,f299,f300,f301
  f314: plane 6.57x6.44mm, normal (0,-1,0), area 37.4mm2, adj f305,f306,f307,f308,f309,f310,f311
  f315: plane 24.34x0.6mm, normal (-1,0,0), area 14.6mm2, adj f2,f316,f318,f319
  f316: plane 5.16x0.6mm, normal (0,0,-1), area 3.1mm2, adj f2,f315,f317,f319
  f317: plane 24.34x0.6mm, normal (1,0,0), area 14.6mm2, adj f2,f316,f318,f319
  f318: plane 5.16x0.6mm, normal (0,0,1), area 3.1mm2, adj f2,f315,f317,f319
  f319: plane 24.34x5.16mm, normal (0,-1,0), area 125.6mm2, adj f315,f316,f317,f318
  f320: plane 5.16x0.6mm, normal (0,0,-1), area 3.1mm2, adj f2,f321,f327,f328
  f321: plane 20.05x0.6mm, normal (1,0,0), area 12mm2, adj f2,f320,f322,f328
  f322: plane 6.61x0.6mm, normal (0,0,-1), area 4mm2, adj f2,f321,f323,f328
  f323: plane 4.29x0.6mm, normal (1,0,0), area 2.6mm2, adj f2,f322,f324,f328
  f324: plane 18.38x0.6mm, normal (0,0,1), area 11mm2, adj f2,f323,f325,f328
  f325: plane 4.29x0.6mm, normal (-1,0,0), area 2.6mm2, adj f2,f324,f326,f328
  f326: plane 6.61x0.6mm, normal (0,0,-1), area 4mm2, adj f2,f325,f327,f328
  f327: plane 20.05x0.6mm, normal (-1,0,0), area 12mm2, adj f2,f320,f326,f328
  f328: plane 24.34x18.38mm, normal (0,-1,0), area 182.4mm2, adj f320,f321,f322,f323,f324,f325,f326,f327
  f329: plane 2x0.6mm, normal (0,0,-1), area 1.2mm2, adj f0,f1,f7,f345
  f330: plane 2x0.6mm, normal (0,0,-1), area 1.2mm2, adj f1,f11,f331,f344
  f331: plane 140x4.8mm, normal (-1,0,0), area 564mm2, adj f1,f330,f332,f335,f336,f337,f339,f344
  f332: cylinder r=8mm len=8mm, axis (0,-1,0), area 60.3mm2, adj f1,f331,f333,f335
  f333: plane 294x4.8mm, normal (0,0,-1), area 1411.2mm2, adj f1,f332,f334,f335
  f334: cylinder r=8mm len=8mm, axis (0,-1,0), area 60.3mm2, adj f0,f1,f333,f335
  f335: plane 314x145.8mm, normal (0,1,0), area 1778mm2, adj f0,f5,f6,f7,f11,f20,f331,f332
  f336: plane 5.96x5mm, normal (-0.77,0,0.64), area 12.4mm2, adj f331,f335,f338,f339
  f337: plane 5x1.6mm, normal (0,0,-1), area 8mm2, adj f331,f335,f338,f339
  f338: plane 56.04x1.6mm, normal (-1,0,0), area 89.7mm2, adj f335,f336,f337,f339
  f339: plane 62x5mm, normal (0,-1,0), area 295.1mm2, adj f331,f336,f337,f338
  f340: plane 5.96x5mm, normal (0.77,0,0.64), area 12.4mm2, adj f0,f335,f341,f343
  f341: plane 56.04x1.6mm, normal (1,0,0), area 89.7mm2, adj f335,f340,f342,f343
  f342: plane 5x1.6mm, normal (0,0,-1), area 8mm2, adj f0,f335,f341,f343
  f343: plane 62x5mm, normal (0,-1,0), area 295.1mm2, adj f0,f340,f341,f342
  f344: plane 4.2x4.2mm, normal (0,0.71,-0.71), area 11.9mm2, adj f11,f330,f331,f335
  f345: plane 4.2x4.2mm, normal (0,0.71,-0.71), area 11.9mm2, adj f0,f7,f329,f335
  f346: cylinder r=7.5mm len=15mm, axis (0,1,0), area 28.3mm2, adj f2,f347
  f347: plane 15x15mm, normal (0,-1,0), area 81.7mm2, adj f36,f346
  f348: cylinder r=7.5mm len=15mm, axis (0,1,0), area 28.3mm2, adj f2,f349
  f349: plane 15x15mm, normal (0,-1,0), area 81.7mm2, adj f35,f348
PLACE A t=(0,3,0)mm
PLACE B t=(0,0,-0.75)mm
MATE fastened B.f36 <-> A.f24  axis (0,1,0) through (-88.5,0,60.75)mm
